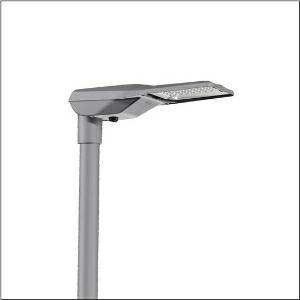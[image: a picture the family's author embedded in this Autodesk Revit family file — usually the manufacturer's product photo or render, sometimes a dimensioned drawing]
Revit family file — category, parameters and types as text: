
# Revit family: streetlight_sl_21_mini___st1_0a_5xe2d33r08hb_bda5
name_source: partatom
category: Lighting Fixtures
units: mm (PartAtom-declared; Revit-internal decimal feet)

## family parameters
Cut with Voids When Loaded = No
Host = Face
Light Source = No
Part Type = Normal
Room Calculation Point = No
Round Connector Dimension = Use Diameter
Shared = No

## types (1)
- --- (1 x LED, 9040 lm, 66 W, 3000K)
    Apparent Load = 66 VA
    CIE Flux Codes = 37 72 97 100 100
    Color Rendering = 70
    Color Temperature = 3000K
    Default Elevation = 1800 mm
    Description = Streetlight SL 21 mini, mast luminaire, primary light control with lens, of PMMA, primary optical cover: cover, of toughened safety glass, transparent, light distribution: ST1.0a, light emission: direct distribution, primary light characteristic: asymmetric, installation type: side-entry, post-top, LED, High Power LED, rated luminous flux: 9.040lm, luminous efficacy: 137lm/W, light colour: 730, colour temperature: 3000K, control gear: D4i, control: flexible luminous flux parameterisation, time-dependent luminous flux control, constant luminous flux control, overheat protection, pre-setting: logarithmic dimming characteristic, mains connection: 220..240V, AC, 50/60Hz, start of lifetime: 66W, end of service life: 69W, reduction: 30W, luminaire housing, of diecast aluminium, powder-coated, SITECO metallic grey (DB 702S), corrosivity category C5 high according to DIN EN ISO 12944, please order mast flange separately, inclination adjustable: 0°, 5°, 10°, 15°, sealing non-destructively replaceable, multi-level sealing system, length: 628mm, width: 235mm, height: 110mm, mast flange for spigot size: 42mm (side-entry): 5XC10008XM4, 60/48mm (side-entry/post-top): 5XC10108XM2, 76/60mm (side-entry/post-top): 5XC10108XM1, mounting height: 4..8m, Smart Interface below, protection rating (complete): IP66, insulation class (complete): insulation class II (safety insulation), certification: CE, ENEC, ENEC+, VDE, impact resistance: IK10, permissible operating ambient temperature for outdoor applications: -40..+50°C, standard-compliant lighting for roads and squares, packaging unit: 1 piece

Light Distribution: ST1.0a
    Height = 110 mm
    Lamp = 1 x LED
    Lamp Light Flux = 9040 lm
    Lamp Power = 66 W
    Lamp count = 1
    Length = 625 mm
    Luminous efficacy = 137 lm/W
    Manufacturer = Siteco
    ModVariant = No
    Model = 5XE2D33R08HB
    Number of Poles = 1
    OnlyDefault = Yes
    Power Factor = 1
    Product Name = Streetlight SL 21 mini | ST1.0a
    Product group = mast luminaire | pylon top
    ProductGroupID = 6100
    Protection Class = Protection class II
    Protection Degree = IP 66
    RLX_Detail_Level = 1
    RLX_Emergency_Light_Flux = 0 lm
    RLX_Emergency_Type = 0
    RLX_Emergency_Type_DB = No
    RlxData = <blob elided: 26281 chars, md5=a7b42b7a>
    Socket = socket
    Standby Power = 0 W
    System Light Flux = 9040 lm
    System Power = 66 W
    Type Comments = factory setting: luminous flux: 100 % | dim-lin: 254 | 670 mA
    Type Image = l_1003516.jpg
    URL = http://relux.com
    VarID = @adj_186231
    Voltage = 0 V
    Weight = 0.00 kg
    Width = 234 mm

## geometry (parser evidence)
native form markers: Blend x4, Sweep x10
no freeform markers — native parametric forms only
